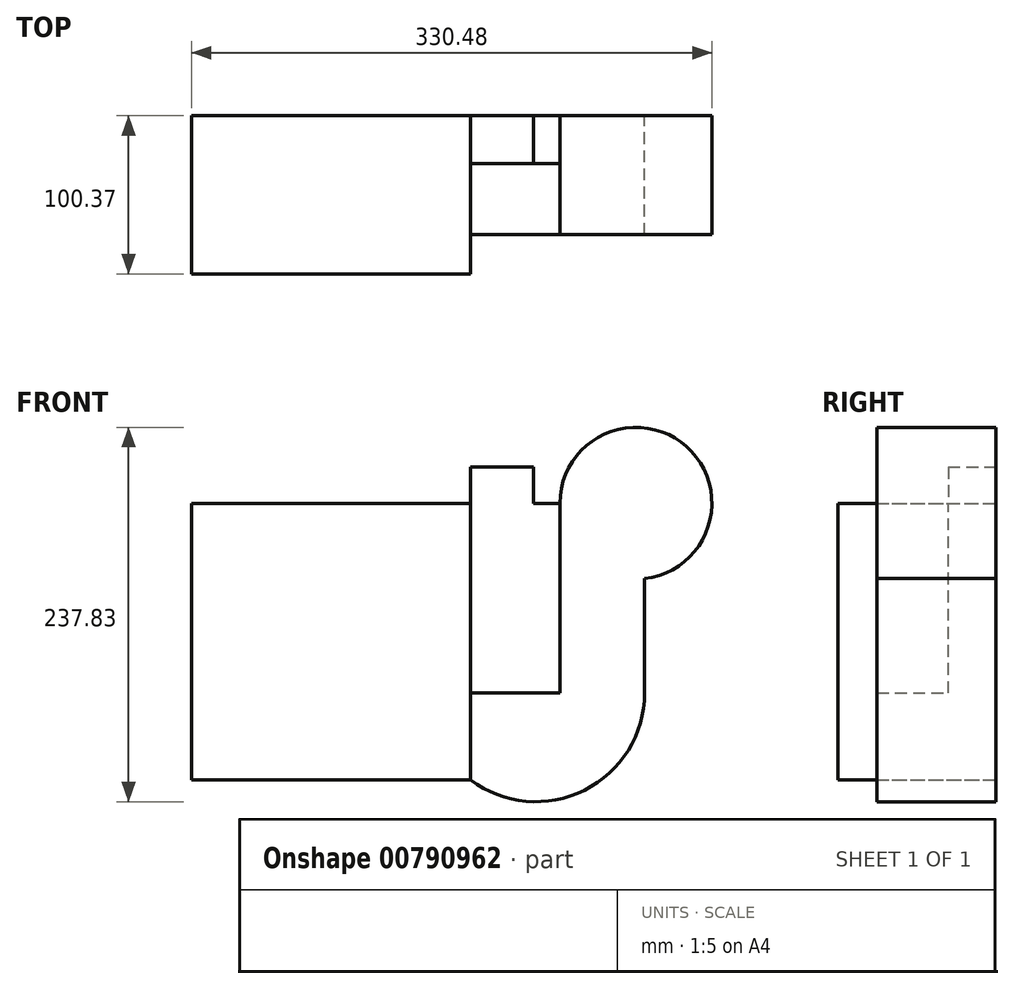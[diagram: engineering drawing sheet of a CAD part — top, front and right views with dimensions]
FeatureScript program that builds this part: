
annotation { "Feature Type Name" : "Feature", "Feature Type Description" : "" }
export const myFeature = defineFeature(function(context is Context, id is Id, definition is map)
    precondition{}
    {
        {
            var Q0;
            Q0=qCreatedBy(makeId("Front.planeOp"),FACE);
            var sketch = newSketch(context, id + "F0", { "sketchPlane" : qUnion([Q0])});
            skLineSegment(sketch, "E0.bottom", {"start": v(88.58, 89) * mm, "end": v(-88.58, 89) * mm});
            skLineSegment(sketch, "E0.top", {"start": v(88.58, -86.72) * mm, "end": v(-88.58, -86.72) * mm});
            skLineSegment(sketch, "E0.left", {"start": v(88.58, 89) * mm, "end": v(88.58, -86.72) * mm});
            skLineSegment(sketch, "E0.right", {"start": v(-88.58, 89) * mm, "end": v(-88.58, -86.72) * mm});
            skLineSegment(sketch, "E1.bottom", {"start": v(128.62, 112.03) * mm, "end": v(88.58, 112.03) * mm});
            skLineSegment(sketch, "E1.top", {"start": v(128.62, 89) * mm, "end": v(88.58, 89) * mm});
            skLineSegment(sketch, "E1.left", {"start": v(128.62, 112.03) * mm, "end": v(128.62, 89) * mm});
            skLineSegment(sketch, "E1.right", {"start": v(88.58, 112.03) * mm, "end": v(88.58, 89) * mm});
            skLineSegment(sketch, "E2.bottom", {"start": v(145.43, -31.53) * mm, "end": v(88.58, -31.53) * mm});
            skLineSegment(sketch, "E2.top", {"start": v(145.43, 89) * mm, "end": v(88.58, 89) * mm});
            skLineSegment(sketch, "E2.left", {"start": v(145.43, -31.53) * mm, "end": v(145.43, 89) * mm});
            skLineSegment(sketch, "E2.right", {"start": v(88.58, -31.53) * mm, "end": v(88.58, 89) * mm});
            skLineSegment(sketch, "E3.bottom", {"start": v(145.43, -31.53) * mm, "end": v(199.16, -31.53) * mm});
            skLineSegment(sketch, "E3.top", {"start": v(145.43, 41.08) * mm, "end": v(199.16, 41.08) * mm});
            skLineSegment(sketch, "E3.left", {"start": v(145.43, -31.53) * mm, "end": v(145.43, 41.08) * mm});
            skLineSegment(sketch, "E3.right", {"start": v(199.16, -31.53) * mm, "end": v(199.16, 41.08) * mm});
            skArc(sketch, "E4", {"start": v(199.16, -31.53) * mm, "mid": v(160.94, -93.32) * mm, "end": v(88.58, -86.72) * mm});
            skArc(sketch, "E5", {"start": v(145.43, 89) * mm, "mid": v(225.77, 125) * mm, "end": v(199.16, 41.08) * mm});
            skSolve(sketch);
        }
        {
            var Q0;
            Q0=makeQuery(id+"F0.imprint","IMPRINT",FACE,{"disambiguationData":[TD([[makeQuery(id+"F0.imprint","IMPRINT",EDGE,{"derivedFrom":sQuery(id+"F0.wireOp",EDGE,"E3.bottom")}),1.0]])]});
            var Q1;
            Q1=makeQuery(id+"F0.imprint","IMPRINT",FACE,{"disambiguationData":[TD([[makeQuery(id+"F0.imprint","IMPRINT",EDGE,{"derivedFrom":sQuery(id+"F0.wireOp",EDGE,"E2.left")}),-1.0]])]});
            var Q2;
            Q2=makeQuery(id+"F0.imprint","IMPRINT",FACE,{"disambiguationData":[TD([[makeQuery(id+"F0.imprint","IMPRINT",EDGE,{"derivedFrom":sQuery(id+"F0.wireOp",EDGE,"E0.left")}),1.0]])]});
            extrude(context, id + "F1", {"entities" : qUnion([Q0, Q1, Q2]), "depth" : 75.48 * mm, "offsetDistance" : 25.4 * mm});
        }
        {
            var Q0;
            Q0=makeQuery(id+"F0.imprint","IMPRINT",FACE,{"disambiguationData":[TD([[makeQuery(id+"F0.imprint","IMPRINT",EDGE,{"derivedFrom":sQuery(id+"F0.wireOp",EDGE,"E2.bottom")}),-1.0]])]});
            var Q1;
            Q1=makeQuery(id+"F0.imprint","IMPRINT",FACE,{"disambiguationData":[TD([[makeQuery(id+"F0.imprint","IMPRINT",EDGE,{"derivedFrom":sQuery(id+"F0.wireOp",EDGE,"E1.bottom")}),1.0]])]});
            var Q2;
            Q2=makeQuery(id+"F0.imprint","IMPRINT",FACE,{"disambiguationData":[TD([[makeQuery(id+"F0.imprint","IMPRINT",EDGE,{"derivedFrom":sQuery(id+"F0.wireOp",EDGE,"E0.left")}),1.0]])]});
            var Q3;
            Q3=makeQuery(id+"F0.imprint","IMPRINT",FACE,{"disambiguationData":[TD([[makeQuery(id+"F0.imprint","IMPRINT",EDGE,{"derivedFrom":sQuery(id+"F0.wireOp",EDGE,"E2.bottom")}),-1.0]])]});
            var Q4;
            Q4=makeQuery(id+"F0.imprint","IMPRINT",FACE,{"disambiguationData":[TD([[makeQuery(id+"F0.imprint","IMPRINT",EDGE,{"derivedFrom":sQuery(id+"F0.wireOp",EDGE,"E1.bottom")}),1.0]])]});
            var Q5;
            Q5=makeQuery(id+"F0.imprint","IMPRINT",FACE,{"disambiguationData":[TD([[makeQuery(id+"F0.imprint","IMPRINT",EDGE,{"derivedFrom":sQuery(id+"F0.wireOp",EDGE,"E2.left")}),-1.0]])]});
            var Q6;
            Q6=makeQuery(id+"F0.imprint","IMPRINT",FACE,{"disambiguationData":[TD([[makeQuery(id+"F0.imprint","IMPRINT",EDGE,{"derivedFrom":sQuery(id+"F0.wireOp",EDGE,"E3.bottom")}),1.0]])]});
            extrude(context, id + "F2", {"entities" : qUnion([Q0, Q1, Q2, Q3, Q4, Q5, Q6]), "operationType" : NewBodyOperationType.ADD, "depth" : 30.23 * mm, "offsetDistance" : 25.4 * mm});
        }
        {
            var Q0;
            Q0=makeQuery(id+"F0.imprint","IMPRINT",FACE,{"disambiguationData":[TD([[makeQuery(id+"F0.imprint","IMPRINT",EDGE,{"derivedFrom":sQuery(id+"F0.wireOp",EDGE,"E0.bottom")}),1.0]])]});
            extrude(context, id + "F3", {"entities" : qUnion([Q0]), "operationType" : NewBodyOperationType.ADD, "depth" : 100.37 * mm, "offsetDistance" : 25.4 * mm});
        }
    });
